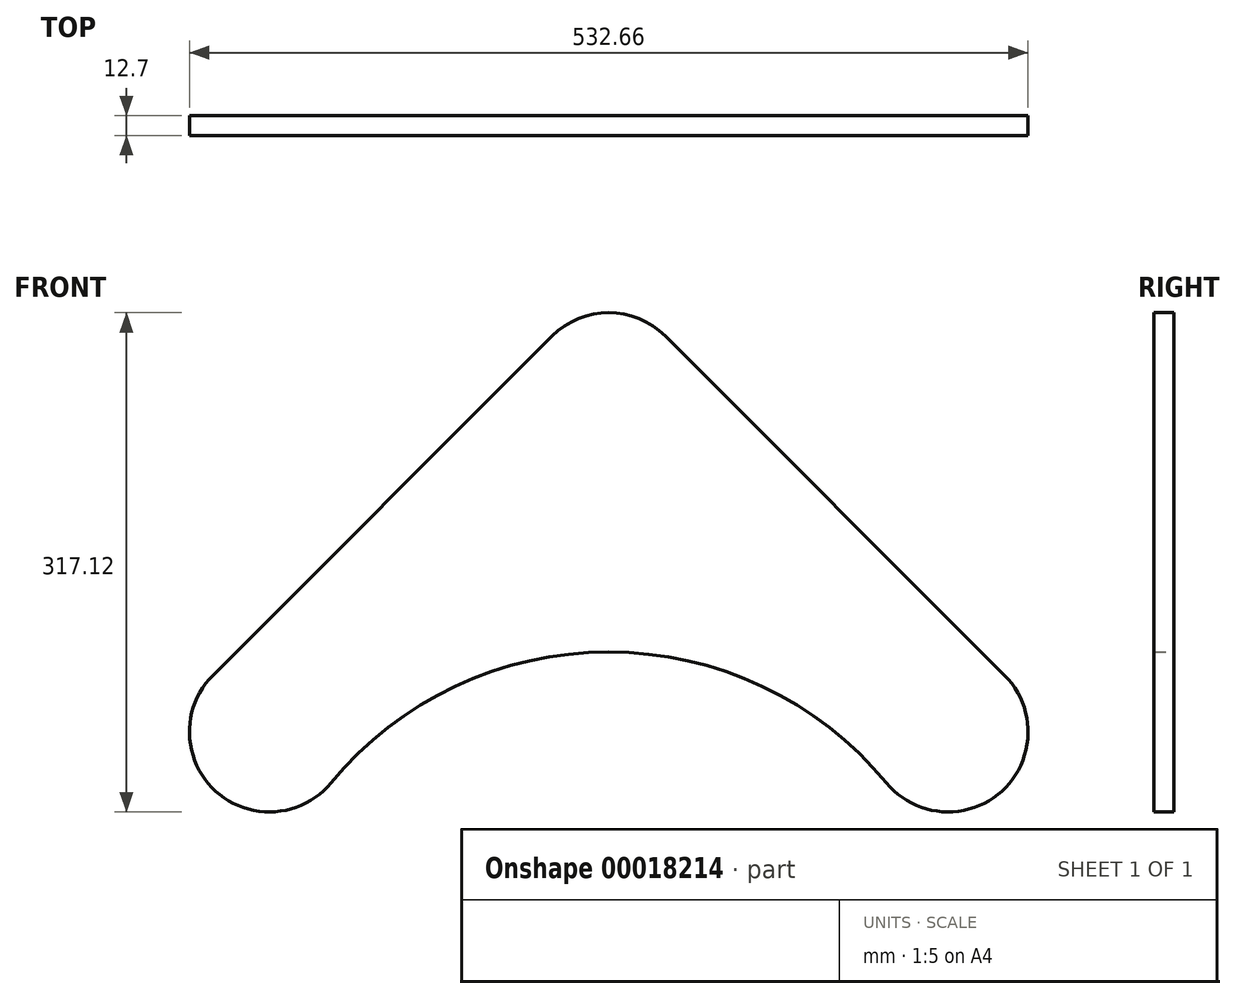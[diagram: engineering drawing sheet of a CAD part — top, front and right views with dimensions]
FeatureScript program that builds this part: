
annotation { "Feature Type Name" : "Feature", "Feature Type Description" : "" }
export const myFeature = defineFeature(function(context is Context, id is Id, definition is map)
    precondition{}
    {
        {
            var Q0;
            Q0=qCreatedBy(makeId("Front.planeOp"),FACE);
            var sketch = newSketch(context, id + "F0", { "sketchPlane" : qUnion([Q0])});
            skCircle(sketch, "E0", {"center": v(0, 0) * mm, "radius": 355.6 * mm, "construction": true});
            skLineSegment(sketch, "E1", {"start": v(-251.45, 251.45) * mm, "end": v(-35.92, 466.97) * mm});
            skLineSegment(sketch, "E2", {"start": v(35.92, 466.97) * mm, "end": v(251.45, 251.45) * mm});
            skArc(sketch, "E3", {"start": v(-251.45, 251.45) * mm, "mid": v(-249.69, 177.93) * mm, "end": v(-176.34, 183.2) * mm});
            skArc(sketch, "E4", {"start": v(176.34, 183.2) * mm, "mid": v(249.69, 177.93) * mm, "end": v(251.45, 251.45) * mm});
            skArc(sketch, "E5.filletArc", {"start": v(35.92, 466.97) * mm, "mid": v(0, 481.85) * mm, "end": v(-35.92, 466.97) * mm});
            skArc(sketch, "E6", {"start": v(176.34, 183.2) * mm, "mid": v(0, 266.33) * mm, "end": v(-176.34, 183.2) * mm});
            skSolve(sketch);
        }
        {
            var Q0;
            Q0=makeQuery(id+"F0.imprint","IMPRINT",FACE,{"disambiguationData":[TD([[makeQuery(id+"F0.imprint","IMPRINT",EDGE,{"derivedFrom":sQuery(id+"F0.wireOp",EDGE,"E1")}),-1.0]])]});
            extrude(context, id + "F1", {"entities" : qUnion([Q0]), "depth" : 12.7 * mm});
        }
    });
